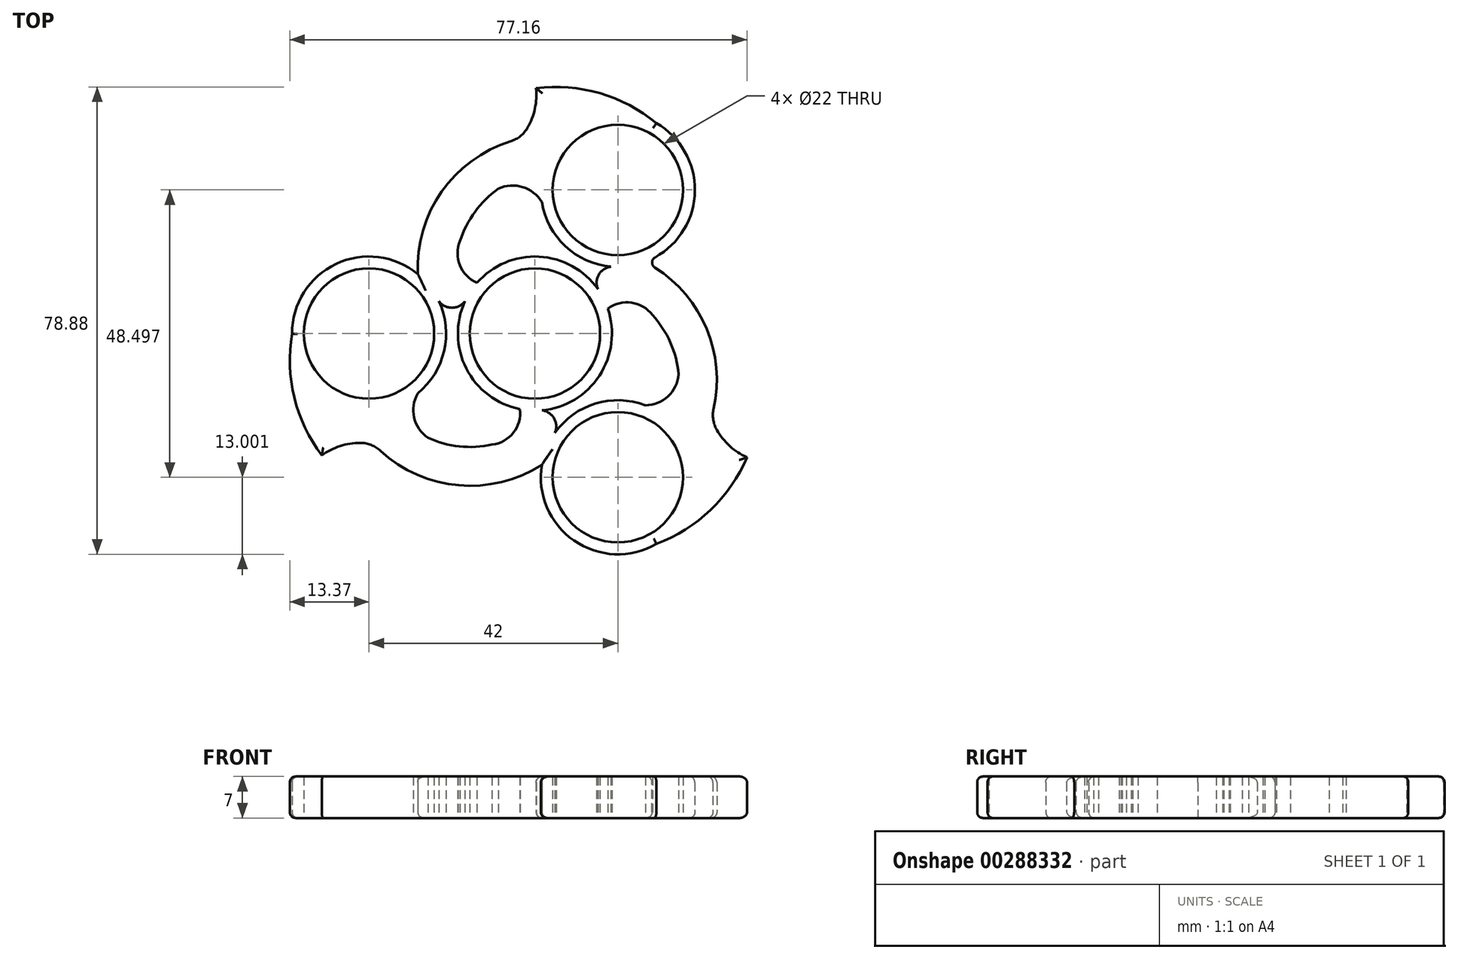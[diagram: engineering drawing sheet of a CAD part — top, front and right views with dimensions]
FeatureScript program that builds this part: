
annotation { "Feature Type Name" : "Feature", "Feature Type Description" : "" }
export const myFeature = defineFeature(function(context is Context, id is Id, definition is map)
    precondition{}
    {
        {
            var Q0;
            Q0=qCreatedBy(makeId("Top.planeOp"),FACE);
            var sketch = newSketch(context, id + "F0", { "sketchPlane" : qUnion([Q0])});
            skCircle(sketch, "E0", {"center": v(0, 0) * mm, "radius": 13 * mm});
            skCircle(sketch, "E1", {"center": v(-28, 0) * mm, "radius": 13 * mm});
            skCircle(sketch, "E2", {"center": v(0, 0) * mm, "radius": 11 * mm});
            skCircle(sketch, "E3", {"center": v(-28, 0) * mm, "radius": 11 * mm});
            skArc(sketch, "E4", {"start": v(-26.07, -19.77) * mm, "mid": v(-12.85, -25.6) * mm, "end": v(1.17, -22.14) * mm});
            skArc(sketch, "E5.trimOffspring", {"start": v(-18.06, -17.59) * mm, "mid": v(-12.74, -19.04) * mm, "end": v(-7.22, -18.74) * mm});
            skArc(sketch, "E6", {"start": v(-29.44, -18.45) * mm, "mid": v(-32.87, -18.98) * mm, "end": v(-35.97, -20.56) * mm});
            skPoint(sketch, "E7.visualSharp", {"position": v(-27.16, -18.7) * mm});
            skArc(sketch, "E7.filletArc", {"start": v(-26.07, -19.77) * mm, "mid": v(-27.63, -18.8) * mm, "end": v(-29.44, -18.45) * mm});
            skArc(sketch, "E8", {"start": v(-19.79, -10.08) * mm, "mid": v(-20.39, -14.17) * mm, "end": v(-18.06, -17.59) * mm});
            skArc(sketch, "E9", {"start": v(-7.22, -18.74) * mm, "mid": v(-3.64, -16.72) * mm, "end": v(-2.53, -12.75) * mm});
            skArc(sketch, "E10", {"start": v(-41, 0) * mm, "mid": v(-40.6, -10.8) * mm, "end": v(-35.97, -20.56) * mm});
            skArc(sketch, "E11", {"start": v(-16.2, 5.46) * mm, "mid": v(-14, 4.36) * mm, "end": v(-11.8, 5.46) * mm});
            skPoint(sketch, "E12.start.orphan", {"position": v(-15, 0) * mm});
            skPoint(sketch, "E13.orphan", {"position": v(-0.12, 12.9) * mm});
            skPoint(sketch, "E14.MirrorCS.end.orphan", {"position": v(-11.8, -5.46) * mm});
            skPoint(sketch, "E14.MirrorCS.start.orphan", {"position": v(-16.2, -5.46) * mm});
            skPoint(sketch, "E15.orphan", {"position": v(-9.7, 8.5) * mm});
            skPoint(sketch, "E16.orphan", {"position": v(1.17, -12.85) * mm});
            skArc(sketch, "E17.1.8", {"start": v(3.38, -16.76) * mm, "mid": v(3.23, -14.3) * mm, "end": v(1.18, -12.95) * mm});
            skPoint(sketch, "E17.2.6", {"position": v(7.5, 13) * mm});
            skPoint(sketch, "E18.1.0", {"position": v(7.5, -13) * mm});
            skArc(sketch, "E18.1.1", {"start": v(18.62, -12.1) * mm, "mid": v(22.47, -10.57) * mm, "end": v(24.26, -6.85) * mm});
            skPoint(sketch, "E18.1.2", {"position": v(12.82, -11.3) * mm});
            skPoint(sketch, "E18.1.3", {"position": v(29.77, -14.18) * mm});
            skPoint(sketch, "E18.1.4", {"position": v(10.62, -7.5) * mm});
            skCircle(sketch, "E18.1.5", {"center": v(14, -24.25) * mm, "radius": 11 * mm});
            skArc(sketch, "E18.1.6", {"start": v(30.7, -16.28) * mm, "mid": v(32.88, -18.98) * mm, "end": v(35.8, -20.87) * mm});
            skCircle(sketch, "E18.1.7", {"center": v(14, -24.25) * mm, "radius": 13 * mm});
            skArc(sketch, "E18.1.8", {"start": v(20.5, -35.5) * mm, "mid": v(29.65, -29.76) * mm, "end": v(35.8, -20.87) * mm});
            skArc(sketch, "E18.1.9", {"start": v(30.16, -12.7) * mm, "mid": v(30.1, -14.54) * mm, "end": v(30.7, -16.28) * mm});
            skArc(sketch, "E18.1.11", {"start": v(24.26, -6.85) * mm, "mid": v(22.86, -1.51) * mm, "end": v(19.85, 3.12) * mm});
            skArc(sketch, "E18.1.12", {"start": v(30.16, -12.7) * mm, "mid": v(28.6, 1.67) * mm, "end": v(18.58, 12.08) * mm});
            skArc(sketch, "E18.1.13", {"start": v(19.85, 3.12) * mm, "mid": v(16.3, 5.2) * mm, "end": v(12.3, 4.18) * mm});
            skArc(sketch, "E18.2.1", {"start": v(1.17, 22.18) * mm, "mid": v(-2.08, 24.74) * mm, "end": v(-6.2, 24.44) * mm});
            skPoint(sketch, "E18.2.2", {"position": v(3.38, 16.76) * mm});
            skPoint(sketch, "E18.2.3", {"position": v(-2.6, 32.87) * mm});
            skPoint(sketch, "E18.2.4", {"position": v(1.18, 12.95) * mm});
            skCircle(sketch, "E18.2.5", {"center": v(14, 24.25) * mm, "radius": 11 * mm});
            skArc(sketch, "E18.2.6", {"start": v(-1.25, 34.72) * mm, "mid": v(0, 37.96) * mm, "end": v(0.18, 41.43) * mm});
            skCircle(sketch, "E18.2.7", {"center": v(14, 24.25) * mm, "radius": 13 * mm});
            skArc(sketch, "E18.2.8", {"start": v(20.5, 35.5) * mm, "mid": v(10.95, 40.56) * mm, "end": v(0.18, 41.43) * mm});
            skArc(sketch, "E18.2.9", {"start": v(-4.09, 32.46) * mm, "mid": v(-2.46, 33.33) * mm, "end": v(-1.25, 34.72) * mm});
            skArc(sketch, "E18.2.10", {"start": v(12.82, 11.3) * mm, "mid": v(10.77, 9.95) * mm, "end": v(10.62, 7.5) * mm});
            skArc(sketch, "E18.2.11", {"start": v(-6.2, 24.44) * mm, "mid": v(-10.12, 20.55) * mm, "end": v(-12.62, 15.63) * mm});
            skArc(sketch, "E18.2.12", {"start": v(-4.09, 32.46) * mm, "mid": v(-15.75, 23.93) * mm, "end": v(-19.76, 10.05) * mm});
            skArc(sketch, "E18.2.13", {"start": v(-12.62, 15.63) * mm, "mid": v(-12.66, 11.51) * mm, "end": v(-9.78, 8.57) * mm});
            skPoint(sketch, "E19.orphan", {"position": v(-19.76, 10.09) * mm});
            skPoint(sketch, "E20.orphan", {"position": v(1.14, -22.16) * mm});
            skPoint(sketch, "E21.orphan", {"position": v(18.62, 12.07) * mm});
            skSolve(sketch);
        }
        {
            var Q0;
            {var subQ3=sQuery(id+"F0.wireOp",EDGE,"E11");Q0=makeQuery(id+"F0.imprint","IMPRINT",FACE,{"disambiguationData":[TD([[makeQuery(id+"F0.imprint","IMPRINT",EDGE,{"derivedFrom":subQ3}),1.0]])]});}
            var Q1;
            Q1=makeQuery(id+"F0.imprint","IMPRINT",FACE,{"disambiguationData":[TD([[makeQuery(id+"F0.imprint","IMPRINT",EDGE,{"derivedFrom":sQuery(id+"F0.wireOp",EDGE,"E3")}),-1.0]])]});
            var Q2;
            {var subQ7=sQuery(id+"F0.wireOp",EDGE,"E4");Q2=makeQuery(id+"F0.imprint","IMPRINT",FACE,{"disambiguationData":[TD([[makeQuery(id+"F0.imprint","IMPRINT",EDGE,{"derivedFrom":subQ7}),1.0]])]});}
            var Q3;
            Q3=makeQuery(id+"F0.imprint","IMPRINT",FACE,{"disambiguationData":[TD([[makeQuery(id+"F0.imprint","IMPRINT",EDGE,{"derivedFrom":sQuery(id+"F0.wireOp",EDGE,"E18.1.5")}),-1.0]])]});
            var Q4;
            {var subQ3=sQuery(id+"F0.wireOp",EDGE,"E18.1.1");Q4=makeQuery(id+"F0.imprint","IMPRINT",FACE,{"disambiguationData":[TD([[makeQuery(id+"F0.imprint","IMPRINT",EDGE,{"derivedFrom":subQ3}),-1.0]])]});}
            var Q5;
            Q5=makeQuery(id+"F0.imprint","IMPRINT",FACE,{"disambiguationData":[TD([[makeQuery(id+"F0.imprint","IMPRINT",EDGE,{"derivedFrom":sQuery(id+"F0.wireOp",EDGE,"E18.2.5")}),-1.0]])]});
            var Q6;
            Q6=makeQuery(id+"F0.imprint","IMPRINT",FACE,{"disambiguationData":[TD([[makeQuery(id+"F0.imprint","IMPRINT",EDGE,{"derivedFrom":sQuery(id+"F0.wireOp",EDGE,"E2")}),-1.0]])]});
            extrude(context, id + "F1", {"entities" : qUnion([Q0, Q1, Q2, Q3, Q4, Q5, Q6]), "depth" : 7 * mm});
        }
        {
            var Q0;
            Q0=makeQuery(id+"F1.opExtrude","CAP_EDGE",EDGE,{"disambiguationData":[OSD([sQuery(id+"F0.wireOp",EDGE,"E4")])],"isStart":false});
            var Q1;
            {var subQ0=sQuery(id+"F0.wireOp",EDGE,"E18.1.7");Q1=makeQuery(id+"F1.opExtrude","CAP_EDGE",EDGE,{"disambiguationData":[OSD([subQ0]),TDD([makeQuery(id+"F0.imprint","IMPRINT",EDGE,{"disambiguationData":[TD([[makeQuery(id+"F0.imprint","INTERSECT",VERTEX,{"derivedFrom":[sQuery(id+"F0.wireOp",EDGE,"E4"),subQ0]}),-1.0]])],"derivedFrom":subQ0})])],"isStart":false});}
            var Q2;
            {var subQ0=sQuery(id+"F0.wireOp",EDGE,"E18.1.7");Q2=makeQuery(id+"F1.opExtrude","CAP_EDGE",EDGE,{"disambiguationData":[OSD([subQ0]),TDD([makeQuery(id+"F0.imprint","IMPRINT",EDGE,{"disambiguationData":[TD([[makeQuery(id+"F0.imprint","INTERSECT",VERTEX,{"derivedFrom":[sQuery(id+"F0.wireOp",EDGE,"E4"),subQ0]}),-1.0]])],"derivedFrom":subQ0})])],"isStart":true});}
            var Q3;
            Q3=makeQuery(id+"F1.opExtrude","CAP_EDGE",EDGE,{"disambiguationData":[OSD([sQuery(id+"F0.wireOp",EDGE,"E4")])],"isStart":true});
            var Q4;
            Q4=makeQuery(id+"F1.opExtrude","CAP_EDGE",EDGE,{"disambiguationData":[OSD([sQuery(id+"F0.wireOp",EDGE,"E7.filletArc")])],"isStart":false});
            var Q5;
            Q5=makeQuery(id+"F1.opExtrude","CAP_EDGE",EDGE,{"disambiguationData":[OSD([sQuery(id+"F0.wireOp",EDGE,"E7.filletArc")])],"isStart":true});
            var Q6;
            Q6=makeQuery(id+"F1.opExtrude","CAP_EDGE",EDGE,{"disambiguationData":[OSD([sQuery(id+"F0.wireOp",EDGE,"E6")])],"isStart":true});
            var Q7;
            Q7=makeQuery(id+"F1.opExtrude","CAP_EDGE",EDGE,{"disambiguationData":[OSD([sQuery(id+"F0.wireOp",EDGE,"E10")])],"isStart":false});
            var Q8;
            Q8=makeQuery(id+"F1.opExtrude","CAP_EDGE",EDGE,{"disambiguationData":[OSD([sQuery(id+"F0.wireOp",EDGE,"E10")])],"isStart":true});
            var Q9;
            Q9=makeQuery(id+"F1.opExtrude","CAP_EDGE",EDGE,{"disambiguationData":[OSD([sQuery(id+"F0.wireOp",EDGE,"E6")])],"isStart":false});
            var Q10;
            Q10=makeQuery(id+"F1.opExtrude","CAP_EDGE",EDGE,{"disambiguationData":[OSD([sQuery(id+"F0.wireOp",EDGE,"E18.1.8")])],"isStart":false});
            var Q11;
            Q11=makeQuery(id+"F1.opExtrude","CAP_EDGE",EDGE,{"disambiguationData":[OSD([sQuery(id+"F0.wireOp",EDGE,"E18.1.8")])],"isStart":true});
            var Q12;
            Q12=makeQuery(id+"F1.opExtrude","CAP_EDGE",EDGE,{"disambiguationData":[OSD([sQuery(id+"F0.wireOp",EDGE,"E18.1.6")])],"isStart":false});
            var Q13;
            Q13=makeQuery(id+"F1.opExtrude","CAP_EDGE",EDGE,{"disambiguationData":[OSD([sQuery(id+"F0.wireOp",EDGE,"E18.1.6")])],"isStart":true});
            var Q14;
            Q14=makeQuery(id+"F1.opExtrude","CAP_EDGE",EDGE,{"disambiguationData":[OSD([sQuery(id+"F0.wireOp",EDGE,"E18.1.9")])],"isStart":true});
            var Q15;
            Q15=makeQuery(id+"F1.opExtrude","CAP_EDGE",EDGE,{"disambiguationData":[OSD([sQuery(id+"F0.wireOp",EDGE,"E18.1.9")])],"isStart":false});
            var Q16;
            Q16=makeQuery(id+"F1.opExtrude","SWEPT_FACE",FACE,{"disambiguationData":[OSD([sQuery(id+"F0.wireOp",EDGE,"E18.1.12")])]});
            var Q17;
            {var subQ0=sQuery(id+"F0.wireOp",EDGE,"E18.2.7");Q17=makeQuery(id+"F1.opExtrude","CAP_EDGE",EDGE,{"disambiguationData":[OSD([subQ0]),TDD([makeQuery(id+"F0.imprint","IMPRINT",EDGE,{"disambiguationData":[TD([[makeQuery(id+"F0.imprint","INTERSECT",VERTEX,{"derivedFrom":[sQuery(id+"F0.wireOp",EDGE,"E18.1.12"),subQ0]}),-1.0]])],"derivedFrom":subQ0})])],"isStart":true});}
            var Q18;
            {var subQ0=sQuery(id+"F0.wireOp",EDGE,"E1");Q18=makeQuery(id+"F1.opExtrude","CAP_EDGE",EDGE,{"disambiguationData":[OSD([subQ0]),TDD([makeQuery(id+"F0.imprint","IMPRINT",EDGE,{"disambiguationData":[TD([[makeQuery(id+"F0.imprint","INTERSECT",VERTEX,{"derivedFrom":[subQ0,sQuery(id+"F0.wireOp",EDGE,"E10")]}),1.0]])],"derivedFrom":subQ0})])],"isStart":false});}
            var Q19;
            Q19=makeQuery(id+"F1.opExtrude","CAP_EDGE",EDGE,{"disambiguationData":[OSD([sQuery(id+"F0.wireOp",EDGE,"E18.2.12")])],"isStart":false});
            var Q20;
            {var subQ0=sQuery(id+"F0.wireOp",EDGE,"E1");Q20=makeQuery(id+"F1.opExtrude","CAP_EDGE",EDGE,{"disambiguationData":[OSD([subQ0]),TDD([makeQuery(id+"F0.imprint","IMPRINT",EDGE,{"disambiguationData":[TD([[makeQuery(id+"F0.imprint","INTERSECT",VERTEX,{"derivedFrom":[subQ0,sQuery(id+"F0.wireOp",EDGE,"E10")]}),1.0]])],"derivedFrom":subQ0})])],"isStart":true});}
            var Q21;
            Q21=makeQuery(id+"F1.opExtrude","CAP_EDGE",EDGE,{"disambiguationData":[OSD([sQuery(id+"F0.wireOp",EDGE,"E18.2.12")])],"isStart":true});
            var Q22;
            Q22=makeQuery(id+"F1.opExtrude","CAP_EDGE",EDGE,{"disambiguationData":[OSD([sQuery(id+"F0.wireOp",EDGE,"E18.2.9")])],"isStart":true});
            var Q23;
            Q23=makeQuery(id+"F1.opExtrude","CAP_EDGE",EDGE,{"disambiguationData":[OSD([sQuery(id+"F0.wireOp",EDGE,"E18.2.9")])],"isStart":false});
            var Q24;
            Q24=makeQuery(id+"F1.opExtrude","CAP_EDGE",EDGE,{"disambiguationData":[OSD([sQuery(id+"F0.wireOp",EDGE,"E18.2.6")])],"isStart":false});
            var Q25;
            Q25=makeQuery(id+"F1.opExtrude","CAP_EDGE",EDGE,{"disambiguationData":[OSD([sQuery(id+"F0.wireOp",EDGE,"E18.2.6")])],"isStart":true});
            var Q26;
            Q26=makeQuery(id+"F1.opExtrude","CAP_EDGE",EDGE,{"disambiguationData":[OSD([sQuery(id+"F0.wireOp",EDGE,"E18.2.8")])],"isStart":true});
            var Q27;
            Q27=makeQuery(id+"F1.opExtrude","CAP_EDGE",EDGE,{"disambiguationData":[OSD([sQuery(id+"F0.wireOp",EDGE,"E18.2.8")])],"isStart":false});
            var Q28;
            {var subQ0=sQuery(id+"F0.wireOp",EDGE,"E18.2.7");Q28=makeQuery(id+"F1.opExtrude","CAP_EDGE",EDGE,{"disambiguationData":[OSD([subQ0]),TDD([makeQuery(id+"F0.imprint","IMPRINT",EDGE,{"disambiguationData":[TD([[makeQuery(id+"F0.imprint","INTERSECT",VERTEX,{"derivedFrom":[sQuery(id+"F0.wireOp",EDGE,"E18.1.12"),subQ0]}),-1.0]])],"derivedFrom":subQ0})])],"isStart":false});}
            fillet(context, id + "F2", {"entities" : qUnion([Q0, Q1, Q2, Q3, Q4, Q5, Q6, Q7, Q8, Q9, Q10, Q11, Q12, Q13, Q14, Q15, Q16, Q17, Q18, Q19, Q20, Q21, Q22, Q23, Q24, Q25, Q26, Q27, Q28]), "radius" : 1 * mm, "tangentPropagation" : true, "allowEdgeOverflow" : false});
        }
    });
